AUTODESK INVENTOR PART (.ipt)
format: ipt  version: 2017 (Build 210142000, 142)  size: 150,528 bytes
history: native  units: mm
features: other x45, extrude x5, sketch x4, plane x2, mirror x2, projected_geometry x2, revolve x1
ambient origin geometry x7: Origin, YZ Plane, XZ Plane, X Axis, Y Axis, Z Axis, Center Point
bodies: Solid1 (feature_tree)
feature tree (61):
  other  "Table"
  other  "StandingElectricalCabinet1800x800x500mm2Doors"
  other  "StandingElectricalCabinet1800x800x600mm2Doors"
  other  "StandingElectricalCabinet1800x1000x400mm2Doors"
  other  "StandingElectricalCabinet2000x1000x400mm2Doors"
  other  "StandingElectricalCabinet2000x1000x500mm2Doors"
  other  "StandingElectricalCabinet2000x1000x600mm2Doors"
  other  "StandingElectricalCabinet1200x1200x500mm2Doors"
  other  "StandingElectricalCabinet1400x1200x500mm2Doors"
  other  "StandingElectricalCabinet1600x1200x500mm2Doors"
  other  "StandingElectricalCabinet1800x1200x400mm2Doors"
  other  "StandingElectricalCabinet1800x1200x500mm2Doors"
  other  "StandingElectricalCabinet1800x1200x600mm2Doors"
  other  "StandingElectricalCabinet2000x1200x400mm2Doors"
  other  "StandingElectricalCabinet2000x1200x500mm2Doors"
  other  "StandingElectricalCabinet2000x1200x600mm2Doors"
  other  "StandingElectricalCabinet2000x1200x800mm2Doors"
  other  "StandingElectricalCabinet1800x400x500mm1Door"
  other  "StandingElectricalCabinet1800x400x600mm1Door"
  other  "StandingElectricalCabinet2000x400x500mm1Door"
  other  "StandingElectricalCabinet2000x400x600mm1Door"
  other  "StandingElectricalCabinet1200x600x500mm1Door"
  other  "StandingElectricalCabinet1400x600x500mm1Door"
  other  "StandingElectricalCabinet1600x600x500mm1Door"
  other  "StandingElectricalCabinet1800x600x400mm1Door"
  other  "StandingElectricalCabinet1800x600x500mm1Door"
  other  "StandingElectricalCabinet2000x600x400mm1Door"
  other  "StandingElectricalCabinet2000x600x500mm1Door"
  other  "StandingElectricalCabinet2000x600x600mm1Door"
  other  "StandingElectricalCabinet2000x600x800mm1Door"
  other  "StandingElectricalCabinet2200x600x800mm1Door"
  other  "StandingElectricalCabinet1200x800x500mm1Door"
  other  "StandingElectricalCabinet1400x800x500mm1Door"
  other  "StandingElectricalCabinet1600x800x500mm1Door"
  other  "StandingElectricalCabinet1800x800x400mm1Door"
  other  "StandingElectricalCabinet1800x800x500mm1Door"
  other  "StandingElectricalCabinet2000x800x400mm1Door"
  other  "StandingElectricalCabinet2000x800x500mm1Door"
  other  "StandingElectricalCabinet2000x800x600mm1Door"
  other  "StandingElectricalCabinet2000x800x800mm1Door"
  other  "StandingElectricalCabinet2200x800x800mm1Door"
  other  "StandingElectricalCabinet1800x1000x400mm1Door"
  other  "FirstSketch"
  extrude  "Extrusion1"  TaperAngle=0.0deg  [1 undecoded]
  extrude  "Extrusion2"  TaperAngle=0.0deg  [1 undecoded]
  extrude  "Extrusion3"  Depth=20.0mm TaperAngle=0.0deg
  extrude  "Extrusion4"  Depth=50.0mm
  plane  "Work Plane1"
  revolve  "Revolution1"  [1 undecoded]
  mirror  "Mirror1"
  plane  "Work Plane2"
  mirror  "Mirror2"
  extrude  "Extrusion5"  Depth=20.0mm
  other  "XY Ground Plane"
  sketch  "Sketch4"  dims[d3=10.0mm d6=0.0mm]
  projected_geometry  "Projected Loop1"
  sketch  "Sketch5"  dims[d7=490.0mm d8=0.0mm]
  other  "Work Axis1"
  sketch  "Sketch6"  dims[d9=2.0mm d10=20.0mm d11=0.0mm]
  sketch  "Sketch7"  dims[d12=30.0mm d13=50.0mm d14=50.0mm d15=20.0mm d16=-2.617994mm d17=0.0mm d18=10.0mm d19=15.0mm d20=90.0deg d21=5.0mm d22=20.0mm d23=0.0mm d24=10.0mm d25=0.0mm]
  projected_geometry  "Projected Loop2"
note: 3 required parameter values undecoded (feature->parameter linkage not recoverable at this tier; creation-order binding heuristic only, values carry confidence <= 0.55)